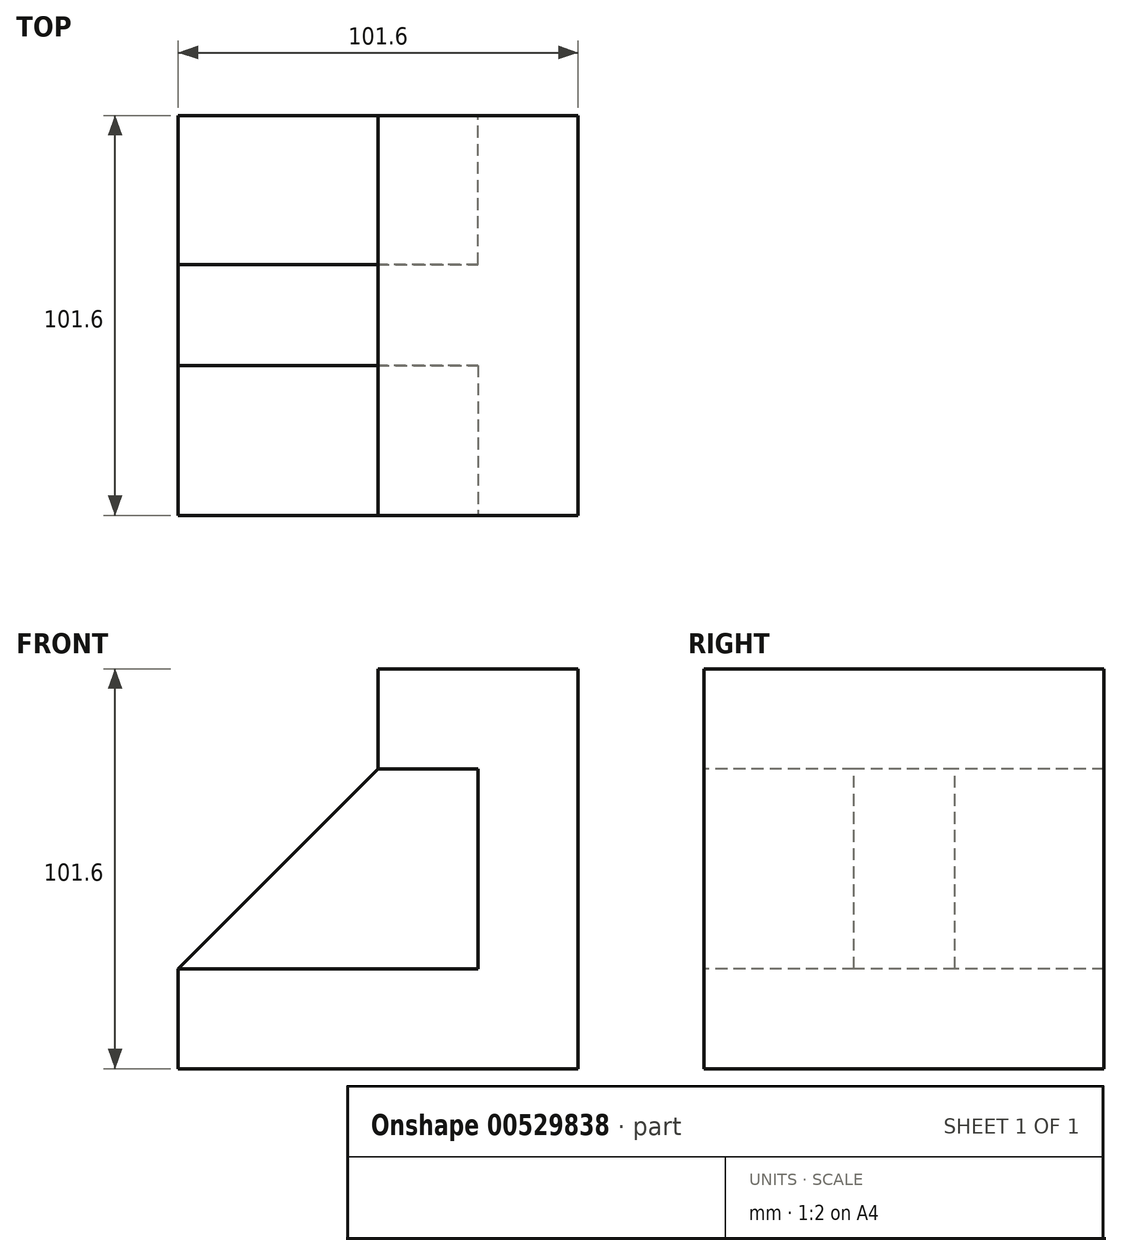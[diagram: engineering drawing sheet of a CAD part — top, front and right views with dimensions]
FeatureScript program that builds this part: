
annotation { "Feature Type Name" : "Feature", "Feature Type Description" : "" }
export const myFeature = defineFeature(function(context is Context, id is Id, definition is map)
    precondition{}
    {
        {
            var Q0;
            Q0=qCreatedBy(makeId("Front.planeOp"),FACE);
            var sketch = newSketch(context, id + "F0", { "sketchPlane" : qUnion([Q0])});
            skLineSegment(sketch, "E0", {"start": v(160.08, 55.13) * mm, "end": v(160.08, -46.47) * mm});
            skLineSegment(sketch, "E1", {"start": v(160.08, -46.47) * mm, "end": v(58.48, -46.47) * mm});
            skLineSegment(sketch, "E2", {"start": v(58.48, -46.47) * mm, "end": v(58.48, -21.07) * mm});
            skLineSegment(sketch, "E3", {"start": v(58.48, -21.07) * mm, "end": v(134.68, -21.07) * mm});
            skLineSegment(sketch, "E4", {"start": v(134.68, -21.07) * mm, "end": v(134.68, 29.73) * mm});
            skLineSegment(sketch, "E5", {"start": v(134.68, 29.73) * mm, "end": v(109.28, 29.73) * mm});
            skLineSegment(sketch, "E6", {"start": v(109.28, 29.73) * mm, "end": v(109.28, 55.13) * mm});
            skLineSegment(sketch, "E7", {"start": v(109.28, 55.13) * mm, "end": v(160.08, 55.13) * mm});
            skLineSegment(sketch, "E8", {"start": v(109.28, 29.73) * mm, "end": v(58.48, -21.07) * mm});
            skSolve(sketch);
        }
        {
            var Q0;
            Q0=makeQuery(id+"F0.imprint","IMPRINT",FACE,{"disambiguationData":[TD([[makeQuery(id+"F0.imprint","IMPRINT",EDGE,{"derivedFrom":sQuery(id+"F0.wireOp",EDGE,"E0")}),-1.0]])]});
            extrude(context, id + "F1", {"entities" : qUnion([Q0]), "oppositeDirection" : true, "depth" : 101.6 * mm, "offsetDistance" : 25.4 * mm});
        }
        {
            var Q0;
            Q0=makeQuery(id+"F1.opExtrude","CAP_FACE",FACE,{"disambiguationData":[OSD([sQuery(id+"F0.wireOp",EDGE,"E0"),sQuery(id+"F0.wireOp",EDGE,"E1"),sQuery(id+"F0.wireOp",EDGE,"E2"),sQuery(id+"F0.wireOp",EDGE,"E3"),sQuery(id+"F0.wireOp",EDGE,"E5"),sQuery(id+"F0.wireOp",EDGE,"E6"),sQuery(id+"F0.wireOp",EDGE,"E7"),sQuery(id+"F0.wireOp",EDGE,"E4")])],"isStart":true});
            var sketch = newSketch(context, id + "F2", { "sketchPlane" : qUnion([Q0])});
            skLineSegment(sketch, "E9", {"start": v(58.48, -21.07) * mm, "end": v(109.28, 29.73) * mm});
            skLineSegment(sketch, "E10", {"start": v(109.28, 29.73) * mm, "end": v(134.68, 29.73) * mm});
            skLineSegment(sketch, "E11", {"start": v(134.68, 29.73) * mm, "end": v(134.68, -21.07) * mm});
            skLineSegment(sketch, "E12", {"start": v(134.68, -21.07) * mm, "end": v(58.48, -21.07) * mm});
            skSolve(sketch);
        }
        {
            var Q0;
            Q0=makeQuery(id+"F2.imprint","IMPRINT",FACE,{"disambiguationData":[TD([[makeQuery(id+"F2.imprint","IMPRINT",EDGE,{"derivedFrom":sQuery(id+"F2.wireOp",EDGE,"E9")}),-1.0]])]});
            extrude(context, id + "F3", {"entities" : qUnion([Q0]), "operationType" : NewBodyOperationType.ADD, "oppositeDirection" : true, "depth" : 101.85 * mm, "offsetDistance" : 25.4 * mm});
        }
        {
            var Q0;
            Q0=makeQuery(id+"F3.boolean.opBoolean","MERGE",FACE,{"derivedFrom":[makeQuery(id+"F1.opExtrude","CAP_FACE",FACE,{"disambiguationData":[OSD([sQuery(id+"F0.wireOp",EDGE,"E0"),sQuery(id+"F0.wireOp",EDGE,"E1"),sQuery(id+"F0.wireOp",EDGE,"E2"),sQuery(id+"F0.wireOp",EDGE,"E3"),sQuery(id+"F0.wireOp",EDGE,"E5"),sQuery(id+"F0.wireOp",EDGE,"E6"),sQuery(id+"F0.wireOp",EDGE,"E7"),sQuery(id+"F0.wireOp",EDGE,"E4")])],"isStart":true}),makeQuery(id+"F3.opExtrude","CAP_FACE",FACE,{"disambiguationData":[OSD([sQuery(id+"F2.wireOp",EDGE,"E9"),sQuery(id+"F2.wireOp",EDGE,"E10"),sQuery(id+"F2.wireOp",EDGE,"E11"),sQuery(id+"F2.wireOp",EDGE,"E12")])],"isStart":true})]});
            var sketch = newSketch(context, id + "F4", { "sketchPlane" : qUnion([Q0])});
            skLineSegment(sketch, "E13", {"start": v(58.48, -21.07) * mm, "end": v(134.68, -21.07) * mm});
            skLineSegment(sketch, "E14", {"start": v(134.68, -21.07) * mm, "end": v(134.68, 29.73) * mm});
            skLineSegment(sketch, "E15", {"start": v(134.68, 29.73) * mm, "end": v(109.28, 29.73) * mm});
            skSolve(sketch);
        }
        {
            var Q0;
            Q0=makeQuery(id+"F4.imprint","IMPRINT",FACE,{"disambiguationData":[TD([[makeQuery(id+"F4.imprint","IMPRINT",EDGE,{"derivedFrom":sQuery(id+"F4.wireOp",EDGE,"E13")}),1.0]])]});
            extrude(context, id + "F5", {"entities" : qUnion([Q0]), "operationType" : NewBodyOperationType.REMOVE, "oppositeDirection" : true, "depth" : 25.4 * mm, "offsetDistance" : 25.4 * mm});
        }
        {
            var Q0;
            Q0=makeQuery(id+"F3.opExtrude","CAP_FACE",FACE,{"disambiguationData":[OSD([sQuery(id+"F2.wireOp",EDGE,"E9"),sQuery(id+"F2.wireOp",EDGE,"E10"),sQuery(id+"F2.wireOp",EDGE,"E11"),sQuery(id+"F2.wireOp",EDGE,"E12")])],"isStart":false});
            extrude(context, id + "F6", {"entities" : qUnion([Q0]), "operationType" : NewBodyOperationType.REMOVE, "oppositeDirection" : true, "depth" : 25.4 * mm, "offsetDistance" : 25.4 * mm});
        }
        {
            var Q0;
            Q0=makeQuery(id+"F5.boolean.opBoolean","COPY",FACE,{"derivedFrom":makeQuery(id+"F5.opExtrude","CAP_FACE",FACE,{"disambiguationData":[OSD([sQuery(id+"F2.wireOp",EDGE,"E9"),sQuery(id+"F4.wireOp",EDGE,"E13"),sQuery(id+"F4.wireOp",EDGE,"E14"),sQuery(id+"F4.wireOp",EDGE,"E15")])],"isStart":false})});
            extrude(context, id + "F7", {"entities" : qUnion([Q0]), "operationType" : NewBodyOperationType.REMOVE, "oppositeDirection" : true, "depth" : 12.7 * mm, "offsetDistance" : 25.4 * mm});
        }
        {
            var Q0;
            Q0=makeQuery(id+"F6.boolean.opBoolean","COPY",FACE,{"derivedFrom":makeQuery(id+"F6.opExtrude","CAP_FACE",FACE,{"disambiguationData":[OSD([sQuery(id+"F2.wireOp",EDGE,"E9"),sQuery(id+"F2.wireOp",EDGE,"E10"),sQuery(id+"F2.wireOp",EDGE,"E11"),sQuery(id+"F2.wireOp",EDGE,"E12")])],"isStart":false})});
            extrude(context, id + "F8", {"entities" : qUnion([Q0]), "operationType" : NewBodyOperationType.REMOVE, "oppositeDirection" : true, "depth" : 12.7 * mm, "offsetDistance" : 25.4 * mm});
        }
    });
